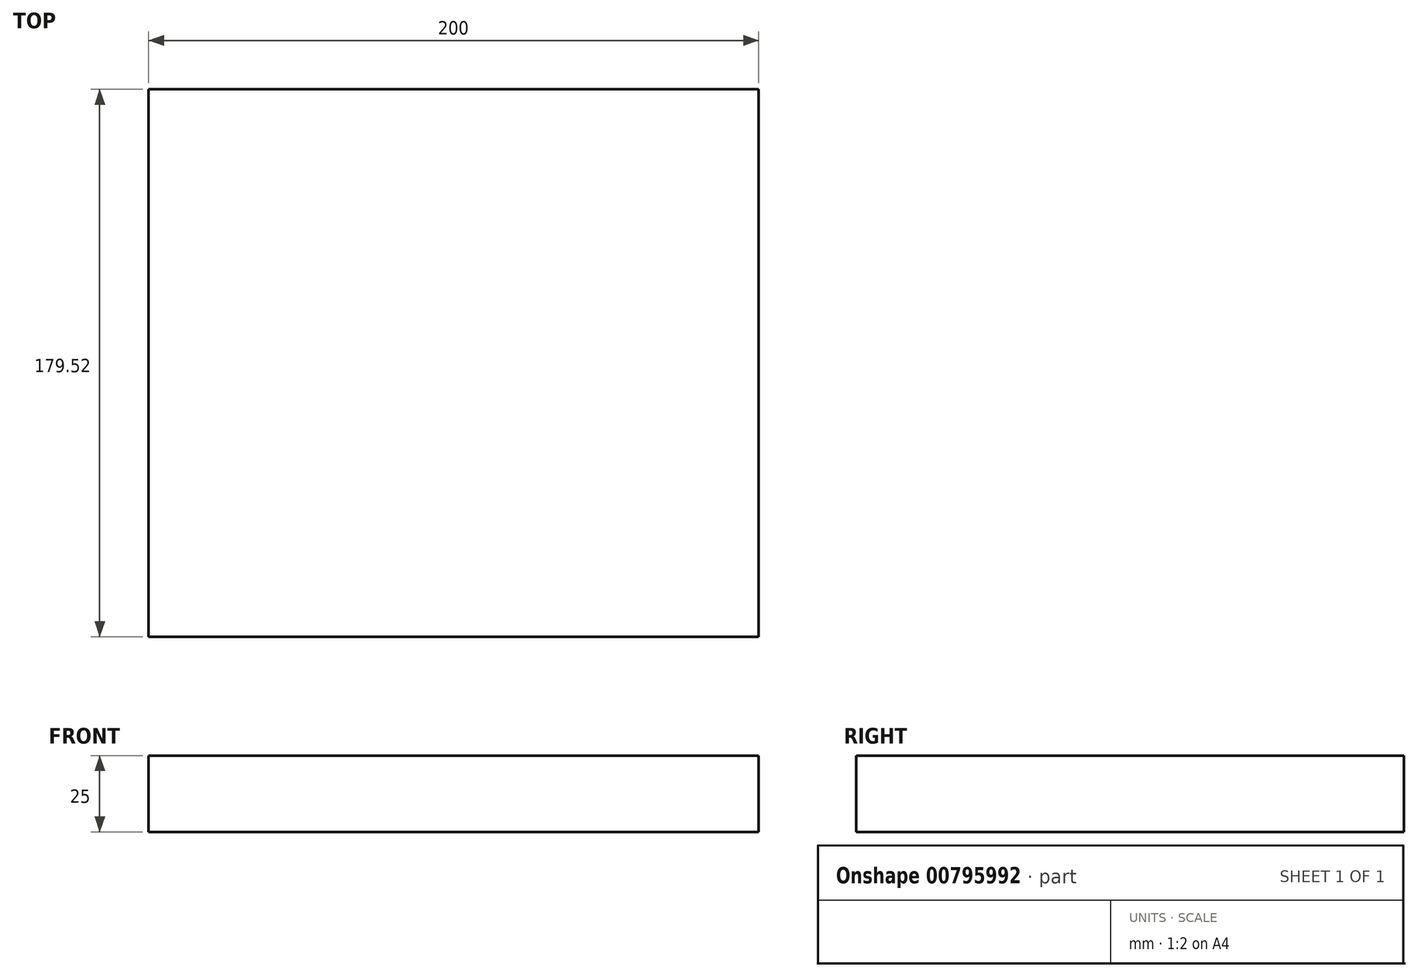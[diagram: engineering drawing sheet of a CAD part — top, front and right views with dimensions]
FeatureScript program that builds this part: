
annotation { "Feature Type Name" : "Feature", "Feature Type Description" : "" }
export const myFeature = defineFeature(function(context is Context, id is Id, definition is map)
    precondition{}
    {
        {
            var Q0;
            Q0=qCreatedBy(makeId("Top.planeOp"),FACE);
            var sketch = newSketch(context, id + "F0", { "sketchPlane" : qUnion([Q0])});
            skLineSegment(sketch, "E0.bottom", {"start": v(0, 0) * mm, "end": v(200, 0) * mm});
            skLineSegment(sketch, "E0.top", {"start": v(0, 179.52) * mm, "end": v(200, 179.52) * mm});
            skLineSegment(sketch, "E0.left", {"start": v(0, 0) * mm, "end": v(0, 179.52) * mm});
            skLineSegment(sketch, "E0.right", {"start": v(200, 0) * mm, "end": v(200, 179.52) * mm});
            skSolve(sketch);
        }
        {
            var Q0;
            Q0 = qSketchRegion(id + "F0", true);
            extrude(context, id + "F1", {"entities" : qUnion([Q0]), "depth" : 25 * mm, "offsetDistance" : 25 * mm});
        }
    });
